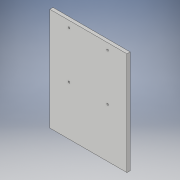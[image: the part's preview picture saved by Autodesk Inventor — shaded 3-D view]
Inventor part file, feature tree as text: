
AUTODESK INVENTOR PART (.ipt)
format: ipt  version: 2019.4 (Build 234330000, 330)  size: 115,200 bytes
history: native  units: in
note: dims shown in document units (in); Inventor stores cm internally (conversion verified against a paired STEP export)
features: extrude x2, sketch x2
ambient origin geometry x8: Origin, YZ Plane, XZ Plane, XY Plane, X Axis, Y Axis, Z Axis, Center Point
bodies: Solid1 (feature_tree)
feature tree (4):
  extrude  "Extrusion1"  Depth=8.0in
  extrude  "Extrusion2"  Depth=0.25in
  sketch  "Sketch1"  dims[d0=6.0in d1=8.0in]
  sketch  "Sketch3"  dims[d2=0.25in d3=0.0in d4=0.135in d7=1.5in d14=0.135in d15=0.135in d16=0.135in d17=3.0in d18=3.65in d19=3.65in d20=3.0in d21=1.5in d22=0.5in d23=0.5in d24=0.25in d25=0.0in]
